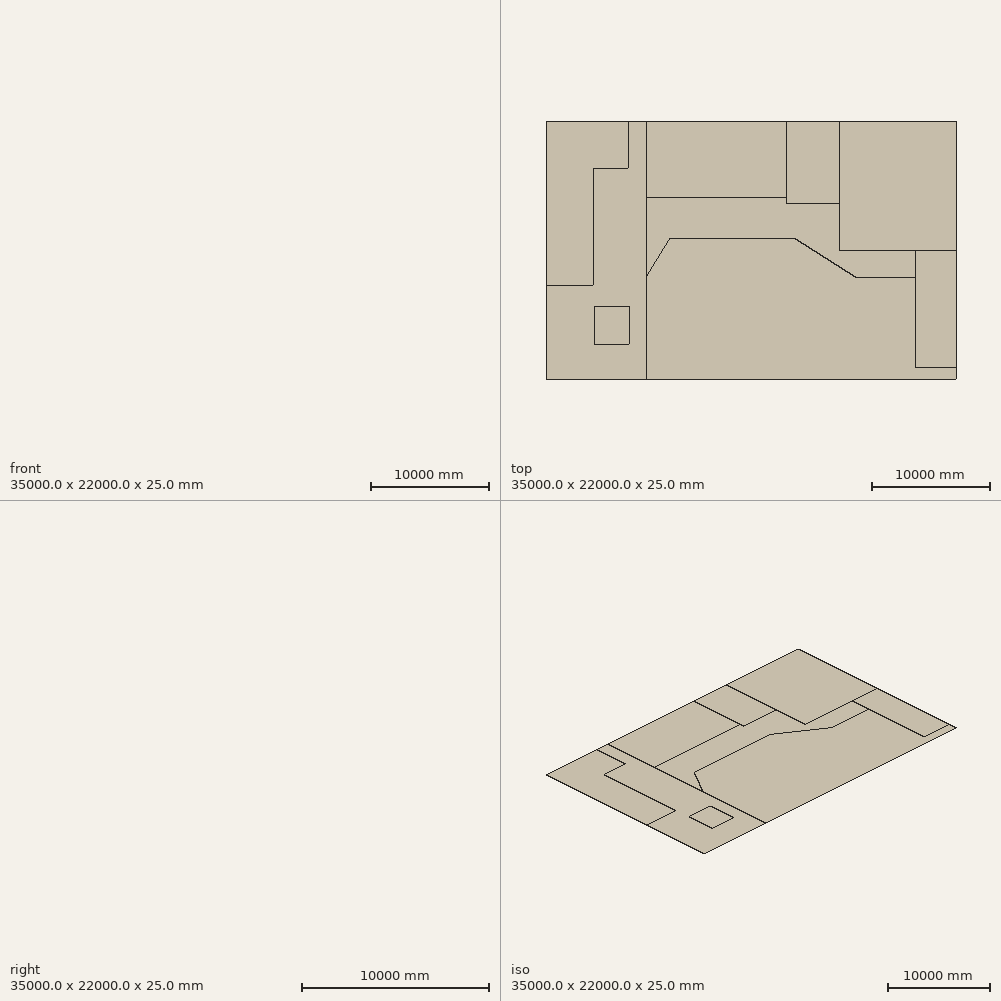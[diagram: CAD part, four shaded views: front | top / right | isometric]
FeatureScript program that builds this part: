
annotation { "Feature Type Name" : "Feature", "Feature Type Description" : "" }
export const myFeature = defineFeature(function(context is Context, id is Id, definition is map)
    precondition{}
    {
        {
            var Q0;
            Q0=qCreatedBy(makeId("Top.planeOp"),FACE);
            var sketch = newSketch(context, id + "F0", { "sketchPlane" : qUnion([Q0])});
            skLineSegment(sketch, "E0.bottom", {"start": v(0, 0) * mm, "end": v(35000, 0) * mm});
            skLineSegment(sketch, "E0.top", {"start": v(0, 35000) * mm, "end": v(35000, 35000) * mm});
            skLineSegment(sketch, "E0.left", {"start": v(0, 0) * mm, "end": v(0, 35000) * mm});
            skLineSegment(sketch, "E0.right", {"start": v(35000, 0) * mm, "end": v(35000, 35000) * mm});
            skLineSegment(sketch, "E1.bottom", {"start": v(8500, 35000) * mm, "end": v(20500, 35000) * mm});
            skLineSegment(sketch, "E1.top", {"start": v(8500, 28500) * mm, "end": v(20500, 28500) * mm});
            skLineSegment(sketch, "E1.left", {"start": v(8500, 35000) * mm, "end": v(8500, 28500) * mm});
            skLineSegment(sketch, "E1.right", {"start": v(20500, 35000) * mm, "end": v(20500, 28500) * mm});
            skLineSegment(sketch, "E2.bottom", {"start": v(35000, 35000) * mm, "end": v(25000, 35000) * mm});
            skLineSegment(sketch, "E2.top", {"start": v(35000, 24000) * mm, "end": v(25000, 24000) * mm});
            skLineSegment(sketch, "E2.left", {"start": v(35000, 35000) * mm, "end": v(35000, 24000) * mm});
            skLineSegment(sketch, "E2.right", {"start": v(25000, 35000) * mm, "end": v(25000, 24000) * mm});
            skLineSegment(sketch, "E3.bottom", {"start": v(20500, 35000) * mm, "end": v(25000, 35000) * mm});
            skLineSegment(sketch, "E3.top", {"start": v(20500, 28000) * mm, "end": v(25000, 28000) * mm});
            skLineSegment(sketch, "E3.left", {"start": v(20500, 35000) * mm, "end": v(20500, 28000) * mm});
            skLineSegment(sketch, "E3.right", {"start": v(25000, 35000) * mm, "end": v(25000, 28000) * mm});
            skLineSegment(sketch, "E4.bottom", {"start": v(35000, 24000) * mm, "end": v(31500, 24000) * mm});
            skLineSegment(sketch, "E4.top", {"start": v(35000, 14000) * mm, "end": v(31500, 14000) * mm});
            skLineSegment(sketch, "E4.left", {"start": v(35000, 24000) * mm, "end": v(35000, 14000) * mm});
            skLineSegment(sketch, "E4.right", {"start": v(31500, 24000) * mm, "end": v(31500, 14000) * mm});
            skLineSegment(sketch, "E5", {"start": v(0, 13000) * mm, "end": v(8500, 13000) * mm});
            skLineSegment(sketch, "E6", {"start": v(8500, 13000) * mm, "end": v(8500, 21694.24) * mm});
            skLineSegment(sketch, "E7", {"start": v(8500, 21694.24) * mm, "end": v(10548.28, 25030.01) * mm});
            skLineSegment(sketch, "E8", {"start": v(10548.28, 25030.01) * mm, "end": v(21187.84, 25030.01) * mm});
            skLineSegment(sketch, "E9", {"start": v(21187.84, 25030.01) * mm, "end": v(26429.76, 21694.24) * mm});
            skLineSegment(sketch, "E10", {"start": v(26429.76, 21694.24) * mm, "end": v(31500, 21694.24) * mm});
            skLineSegment(sketch, "E11", {"start": v(0, 21000) * mm, "end": v(4000, 21000) * mm});
            skLineSegment(sketch, "E12", {"start": v(4000, 21000) * mm, "end": v(4000, 31000) * mm});
            skLineSegment(sketch, "E13", {"start": v(4000, 31000) * mm, "end": v(7000, 31000) * mm});
            skLineSegment(sketch, "E14", {"start": v(7000, 31000) * mm, "end": v(7000, 35000) * mm});
            skLineSegment(sketch, "E15.bottom", {"start": v(4089.12, 19251.99) * mm, "end": v(7067.49, 19251.99) * mm});
            skLineSegment(sketch, "E15.top", {"start": v(4089.12, 15975.78) * mm, "end": v(7067.49, 15975.78) * mm});
            skLineSegment(sketch, "E15.left", {"start": v(4089.12, 19251.99) * mm, "end": v(4089.12, 15975.78) * mm});
            skLineSegment(sketch, "E15.right", {"start": v(7067.49, 19251.99) * mm, "end": v(7067.49, 15975.78) * mm});
            skLineSegment(sketch, "E16", {"start": v(8500, 21694.24) * mm, "end": v(8500, 28500) * mm});
            skLineSegment(sketch, "E17", {"start": v(8500, 13000) * mm, "end": v(35000, 13000) * mm});
            skSolve(sketch);
        }
        {
            var Q0;
            {var subQ0=sQuery(id+"F0.wireOp",EDGE,"E11");Q0=makeQuery(id+"F0.imprint","IMPRINT",FACE,{"disambiguationData":[TD([[makeQuery(id+"F0.imprint","IMPRINT",EDGE,{"derivedFrom":subQ0}),1.0]])]});}
            var Q1;
            Q1=makeQuery(id+"F0.imprint","IMPRINT",FACE,{"disambiguationData":[TD([[makeQuery(id+"F0.imprint","IMPRINT",EDGE,{"derivedFrom":sQuery(id+"F0.wireOp",EDGE,"E15.bottom")}),-1.0]])]});
            var Q2;
            {var subQ4=sQuery(id+"F0.wireOp",EDGE,"E1.right");Q2=makeQuery(id+"F0.imprint","IMPRINT",FACE,{"disambiguationData":[TD([[makeQuery(id+"F0.imprint","IMPRINT",EDGE,{"derivedFrom":subQ4}),1.0]])]});}
            extrude(context, id + "F1", {"entities" : qUnion([Q0, Q1, Q2]), "depth" : 25 * mm, "offsetDistance" : 25 * mm});
        }
        {
            var Q0;
            Q0=makeQuery(id+"F0.imprint","IMPRINT",FACE,{"disambiguationData":[TD([[makeQuery(id+"F0.imprint","IMPRINT",EDGE,{"derivedFrom":sQuery(id+"F0.wireOp",EDGE,"E1.top")}),1.0]])]});
            extrude(context, id + "F2", {"entities" : qUnion([Q0]), "depth" : 25 * mm, "offsetDistance" : 25 * mm});
        }
        {
            var Q0;
            Q0=makeQuery(id+"F0.imprint","IMPRINT",FACE,{"disambiguationData":[TD([[makeQuery(id+"F0.imprint","IMPRINT",EDGE,{"derivedFrom":sQuery(id+"F0.wireOp",EDGE,"E1.top")}),-1.0]])]});
            extrude(context, id + "F3", {"entities" : qUnion([Q0]), "depth" : 25 * mm, "offsetDistance" : 25 * mm});
        }
        {
            var Q0;
            {var subQ4=sQuery(id+"F0.wireOp",EDGE,"E1.left");Q0=makeQuery(id+"F0.imprint","IMPRINT",FACE,{"disambiguationData":[TD([[makeQuery(id+"F0.imprint","IMPRINT",EDGE,{"derivedFrom":subQ4}),-1.0]])]});}
            extrude(context, id + "F4", {"entities" : qUnion([Q0]), "depth" : 25 * mm, "offsetDistance" : 25 * mm});
        }
        {
            var Q0;
            {var subQ2=sQuery(id+"F0.wireOp",EDGE,"E2.right");var subQ5=sQuery(id+"F0.wireOp",EDGE,"E0.top");var subQ8=makeQuery(id+"F0.imprint","INTERSECT",VERTEX,{"derivedFrom":[subQ5,subQ2]});Q0=makeQuery(id+"F0.imprint","IMPRINT",FACE,{"disambiguationData":[TD([[makeQuery(id+"F0.imprint","IMPRINT",EDGE,{"disambiguationData":[TD([[subQ8,-1.0]])],"derivedFrom":subQ5}),-1.0]])]});}
            extrude(context, id + "F5", {"entities" : qUnion([Q0]), "depth" : 25 * mm, "offsetDistance" : 25 * mm});
        }
        {
            var Q0;
            {var subQ1=sQuery(id+"F0.wireOp",EDGE,"E4.top");Q0=makeQuery(id+"F0.imprint","IMPRINT",FACE,{"disambiguationData":[TD([[makeQuery(id+"F0.imprint","IMPRINT",EDGE,{"derivedFrom":subQ1}),-1.0]])]});}
            extrude(context, id + "F6", {"entities" : qUnion([Q0]), "depth" : 25 * mm, "offsetDistance" : 25 * mm});
        }
        {
            var Q0;
            {var subQ1=sQuery(id+"F0.wireOp",EDGE,"E4.top");Q0=makeQuery(id+"F0.imprint","IMPRINT",FACE,{"disambiguationData":[TD([[makeQuery(id+"F0.imprint","IMPRINT",EDGE,{"derivedFrom":subQ1}),1.0]])]});}
            extrude(context, id + "F7", {"entities" : qUnion([Q0]), "depth" : 25 * mm, "offsetDistance" : 25 * mm});
        }
    });
